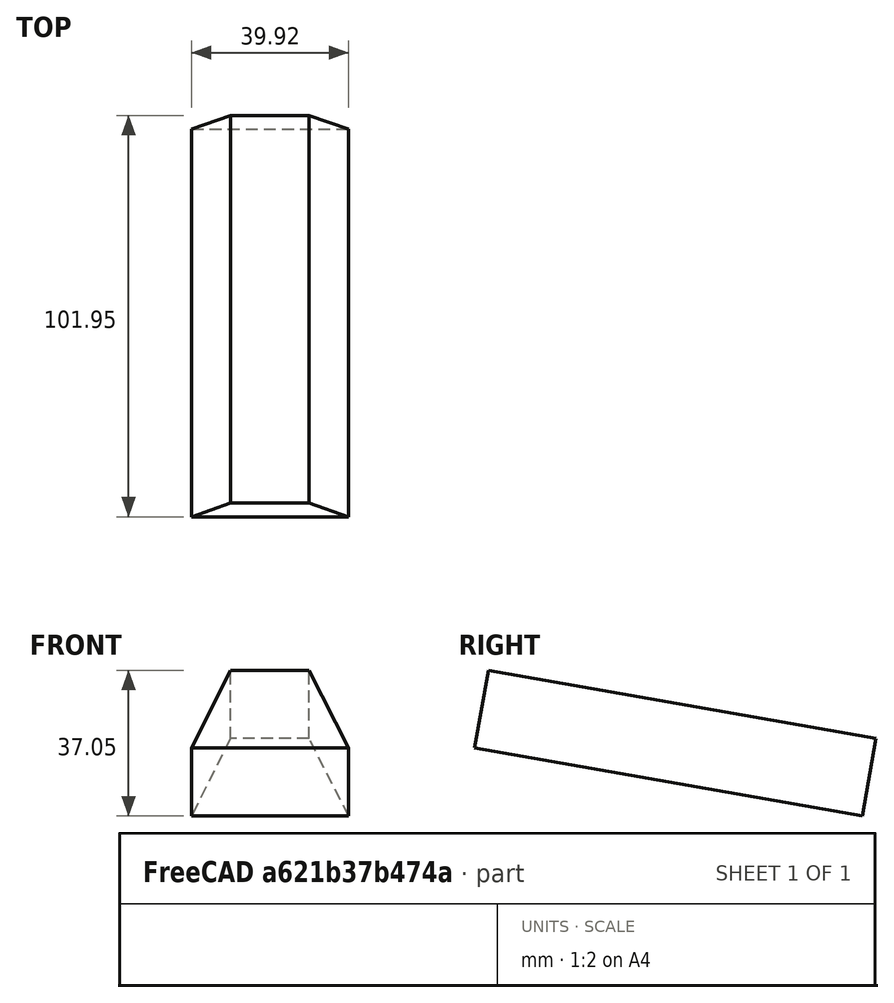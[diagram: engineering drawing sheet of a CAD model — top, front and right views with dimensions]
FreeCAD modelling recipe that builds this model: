
FCSTD DOCUMENT  (FreeCAD 0.21R33694 (Git))
Label: OJT1_T16R01_lingoteoro
License: All rights reserved
LicenseURL: http://en.wikipedia.org/wiki/All_rights_reserved
objects: Sketcher::SketchObject×1, PartDesign::Pad×1, PartDesign::Body×1
note: 4 computed .brp shape members not serialized (recipe doc carries the construction recipe); baked Part::Feature solids carry a one-line shape summary decoded from their .brp

FEATURE [Sketcher::SketchObject] Sketch
  FullyConstrained = false
  MapMode = 5
  Support = -> [XY_Plane]
  sketch-geometry (4):
    g0: LineSegment StartX=-9.97942 StartY=19.99 StartZ=0 EndX=-19.856 EndY=0 EndZ=0
    g1: LineSegment StartX=-19.856 StartY=0 StartZ=0 EndX=20.0617 EndY=0 EndZ=0
    g2: LineSegment StartX=20.0617 StartY=0 StartZ=0 EndX=9.99576 EndY=19.99 EndZ=0
    g3: LineSegment StartX=9.99576 StartY=19.99 StartZ=0 EndX=-9.97942 EndY=19.99 EndZ=0
  constraints (6):
    c: PointOnObject(g0,g-1)
    c: Coincident(g0,g1)
    c: Coincident(g1,g2)
    c: Coincident(g2,g3)
    c: Coincident(g3,g0)
    c: Horizontal(g3)
FEATURE [PartDesign::Pad] Pad
  Direction = (0,0,1)
  Length = 100
  Length2 = 10
  Profile = -> Sketch
  ReferenceAxis = -> Sketch [N_Axis]
  Type = 0
FEATURE [PartDesign::Body] Body
  Group = -> [Sketch,Pad]
  Origin = -> Origin
  Placement = pos=(0,0,0) rot=(1,0,0;1.39626rad)
  Tip = -> Pad
